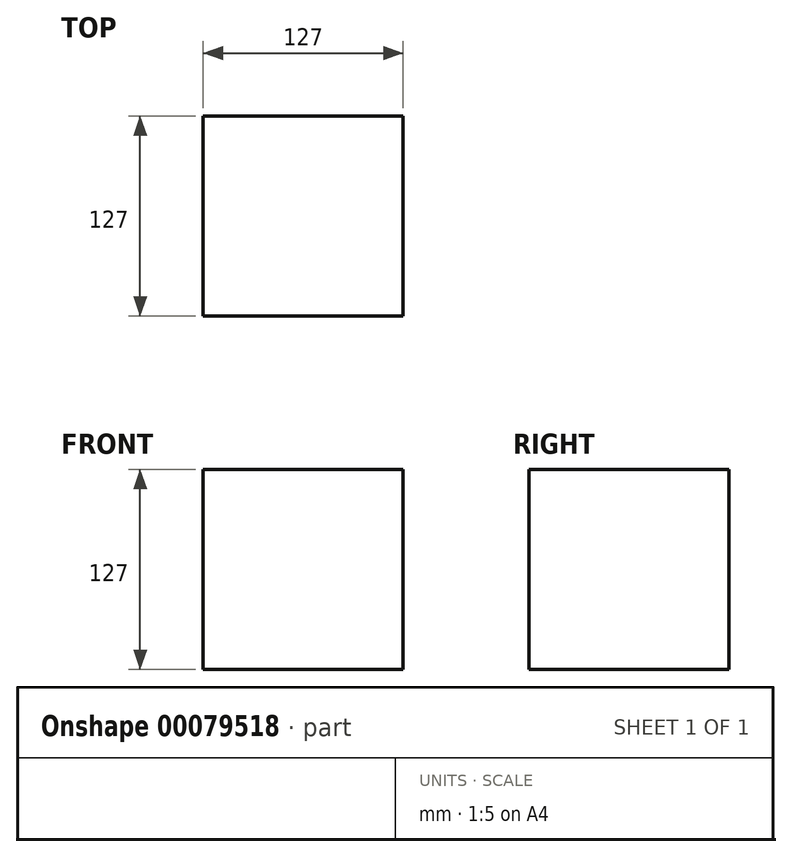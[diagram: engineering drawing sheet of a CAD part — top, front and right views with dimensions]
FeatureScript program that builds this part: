
annotation { "Feature Type Name" : "Feature", "Feature Type Description" : "" }
export const myFeature = defineFeature(function(context is Context, id is Id, definition is map)
    precondition{}
    {
        {
            var Q0;
            Q0=qCreatedBy(makeId("Front.planeOp"),FACE);
            var sketch = newSketch(context, id + "F0", { "sketchPlane" : qUnion([Q0])});
            skLineSegment(sketch, "E0", {"start": v(0, 0) * mm, "end": v(127, 0) * mm});
            skLineSegment(sketch, "E1", {"start": v(127, 0) * mm, "end": v(127, 127) * mm});
            skLineSegment(sketch, "E2", {"start": v(127, 127) * mm, "end": v(0, 127) * mm});
            skLineSegment(sketch, "E3", {"start": v(0, 127) * mm, "end": v(0, 0) * mm});
            skSolve(sketch);
        }
        {
            var Q0;
            Q0=makeQuery(id+"F0.imprint","IMPRINT",FACE,{"disambiguationData":[TD([[makeQuery(id+"F0.imprint","IMPRINT",EDGE,{"derivedFrom":sQuery(id+"F0.wireOp",EDGE,"E0")}),1.0]])]});
            extrude(context, id + "F1", {"entities" : qUnion([Q0]), "depth" : 127 * mm});
        }
    });
